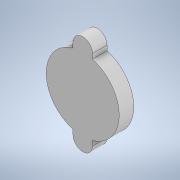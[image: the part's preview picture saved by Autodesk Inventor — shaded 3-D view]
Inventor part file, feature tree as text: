
AUTODESK INVENTOR PART (.ipt)
format: ipt  version: 2021 (Build 250183000, 183)  size: 109,056 bytes
history: native  units: mm
features: extrude x1, fillet x1, mirror x1, sketch x1
ambient origin geometry x8: Origin, YZ Plane, XZ Plane, XY Plane, X Axis, Y Axis, Z Axis, Center Point
bodies: Solid1 (feature_tree)
feature tree (4):
  extrude  "Extrusion1"  Depth=2.0mm
  fillet  "Fillet1"  [1 undecoded]
  mirror  "Mirror1"
  sketch  "Sketch1"  dims[d0=3.0mm d1=0.0mm d2=2.0mm]
note: 1 required parameter value undecoded (feature->parameter linkage not recoverable at this tier; creation-order binding heuristic only, values carry confidence <= 0.55)
